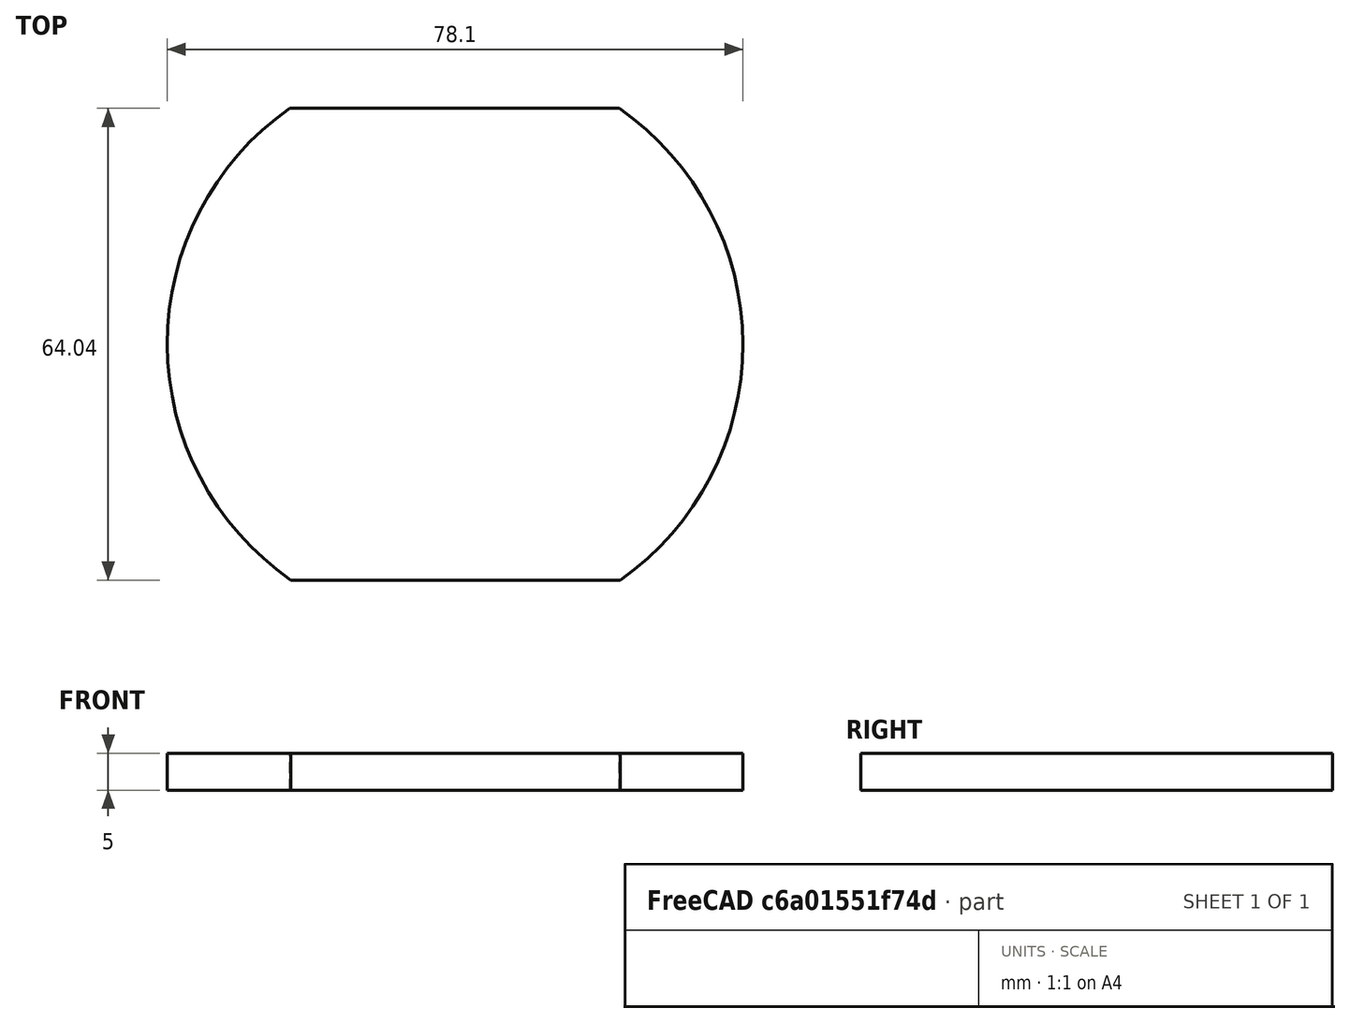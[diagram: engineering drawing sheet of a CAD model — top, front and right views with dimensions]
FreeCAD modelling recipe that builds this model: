
FCSTD DOCUMENT  (FreeCAD 1.0R39319 (Git))
Label: chapa_chord_cut_CORRECTED
License: All rights reserved
LicenseURL: https://en.wikipedia.org/wiki/All_rights_reserved
objects: Sketcher::SketchObject×1, PartDesign::Pad×1, PartDesign::Body×1
note: 6 computed .brp shape members not serialized (recipe doc carries the construction recipe); baked Part::Feature solids carry a one-line shape summary decoded from their .brp

FEATURE [Sketcher::SketchObject] Sketch_1
  ArcFitTolerance = 1e-06
  AttachmentSupport = -> [XY_Plane]
  FullyConstrained = false
  MakeInternals = false
  MapMode = 5
  sketch-geometry (4):
    g0: ArcOfCircle CenterX=-0.00134139 CenterY=-7.04808 CenterZ=0 NormalX=0 NormalY=0 NormalZ=1 AngleXU=0 Radius=39.0492 StartAngle=5.32437 EndAngle=7.24728
    g1: LineSegment StartX=22.263 StartY=25.0321 StartZ=0 EndX=-22.4327 EndY=25.0321 EndZ=0
    g2: ArcOfCircle CenterX=0.00211253 CenterY=-6.92989 CenterZ=0 NormalX=0 NormalY=0 NormalZ=1 AngleXU=0 Radius=39.0499 StartAngle=2.18281 EndAngle=4.10567
    g3: LineSegment StartX=-22.263 StartY=-39.0104 StartZ=0 EndX=22.4319 EndY=-39.0104 EndZ=0
  constraints (7):
    c: Coincident(g0,g1)
    c: Coincident(g1,g2)
    c: Coincident(g2,g3)
    c: Coincident(g3,g0)
    c: Parallel(g1,g3)
    c: Horizontal(g1)
    c: Distance(g1,g3) = 78
FEATURE [PartDesign::Pad] Pad_1
  Direction = (0,0,1)
  Length = 5
  Length2 = 10
  Profile = -> Sketch_1
  Refine = true
  Suppressed = false
  Type = 0
FEATURE [PartDesign::Body] Body
  AllowCompound = false
  Group = -> [Sketch_1,Pad_1]
  Origin = -> Origin
  Tip = -> Pad_1
